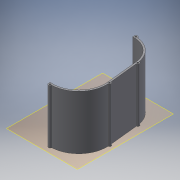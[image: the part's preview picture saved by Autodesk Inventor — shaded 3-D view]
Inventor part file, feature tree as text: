
AUTODESK INVENTOR PART (.ipt)
format: ipt  version: 2017 (Build 210142000, 142)  size: 125,952 bytes
history: native  units: mm
features: other x3, plane x1, extrude x1, sketch x1, reference x1
ambient origin geometry x8: Origin, YZ Plane, XZ Plane, XY Plane, X Axis, Y Axis, Z Axis, Center Point
bodies: Solid1 (feature_tree)
feature tree (7):
  plane  "Work Plane1"
  extrude  "Extrusion1"  Depth=4.0mm
  sketch  "Sketch1"  dims[d0=4.0mm d1=4.0mm d2=135.0mm d3=0.0mm]
  reference  "Reference1"
  parser-record x1  (decoder bookkeeping rows leaked as tree rows — omitted from the tree; the rows remain in map.json)
  other  "gearbox.iam"
  other  "case part 1:1"
note: 1 file-system path scrubbed to <path> (originals preserved in map.json)
